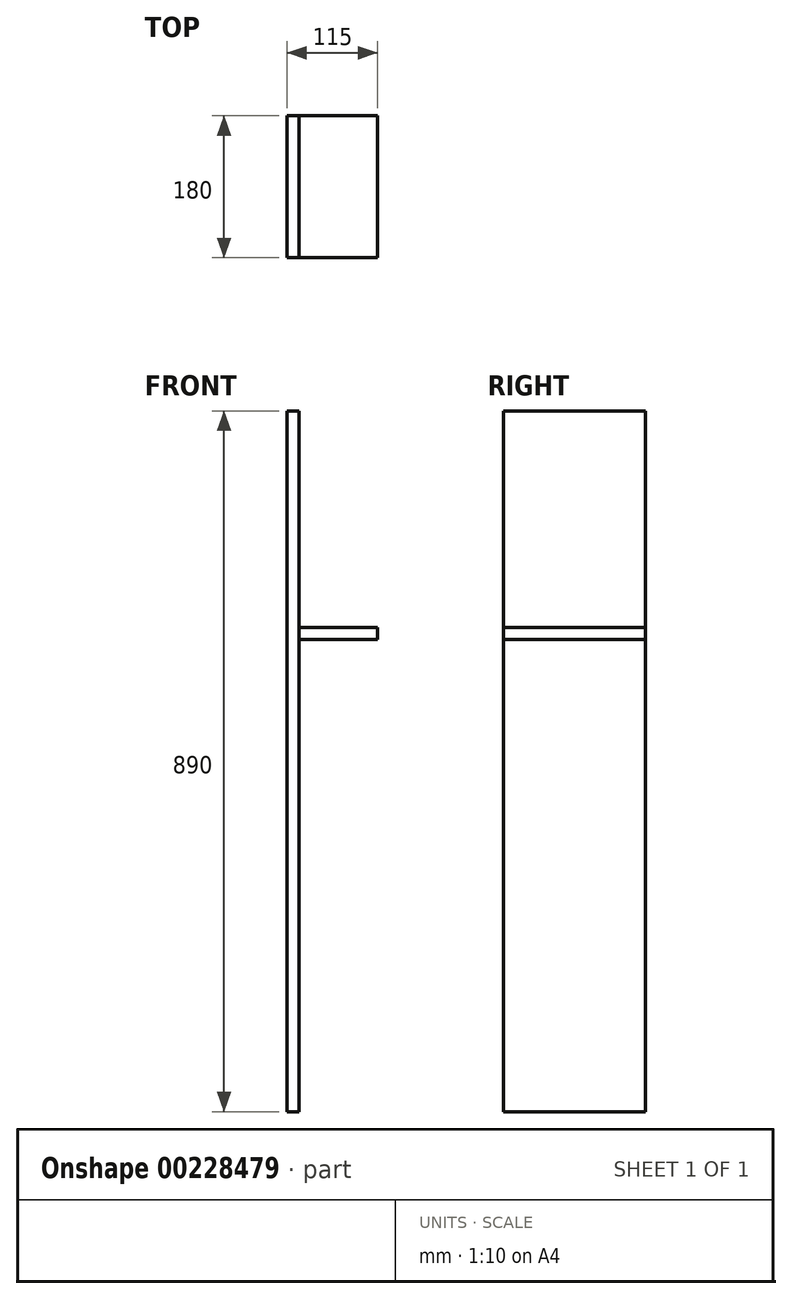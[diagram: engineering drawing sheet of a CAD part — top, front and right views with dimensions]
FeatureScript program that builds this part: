
annotation { "Feature Type Name" : "Feature", "Feature Type Description" : "" }
export const myFeature = defineFeature(function(context is Context, id is Id, definition is map)
    precondition{}
    {
        {
            var Q0;
            Q0=qCreatedBy(makeId("Front.planeOp"),FACE);
            var sketch = newSketch(context, id + "F0", { "sketchPlane" : qUnion([Q0])});
            skLineSegment(sketch, "E0", {"start": v(0, 290) * mm, "end": v(0, 0) * mm});
            skLineSegment(sketch, "E1", {"start": v(0, 0) * mm, "end": v(0, -600) * mm});
            skLineSegment(sketch, "E2", {"start": v(0, -600) * mm, "end": v(15, -600) * mm});
            skLineSegment(sketch, "E3", {"start": v(15, -600) * mm, "end": v(15, 290) * mm});
            skLineSegment(sketch, "E4", {"start": v(15, 290) * mm, "end": v(0, 290) * mm});
            skLineSegment(sketch, "E5", {"start": v(15, 0) * mm, "end": v(115, 0) * mm});
            skLineSegment(sketch, "E6", {"start": v(115, 0) * mm, "end": v(115, 15) * mm});
            skLineSegment(sketch, "E7", {"start": v(115, 15) * mm, "end": v(15, 15) * mm});
            skSolve(sketch);
        }
        {
            var Q0;
            Q0=makeQuery(id+"F0.imprint","IMPRINT",FACE,{"disambiguationData":[TD([[makeQuery(id+"F0.imprint","IMPRINT",EDGE,{"derivedFrom":sQuery(id+"F0.wireOp",EDGE,"E0")}),1.0]])]});
            extrude(context, id + "F1", {"entities" : qUnion([Q0]), "oppositeDirection" : true, "depth" : 180 * mm});
        }
        {
            var Q0;
            {var subQ0=sQuery(id+"F0.wireOp",EDGE,"E5");Q0=makeQuery(id+"F0.imprint","IMPRINT",FACE,{"disambiguationData":[TD([[makeQuery(id+"F0.imprint","IMPRINT",EDGE,{"derivedFrom":subQ0}),1.0]])]});}
            extrude(context, id + "F2", {"entities" : qUnion([Q0]), "oppositeDirection" : true, "depth" : 180 * mm});
        }
    });
